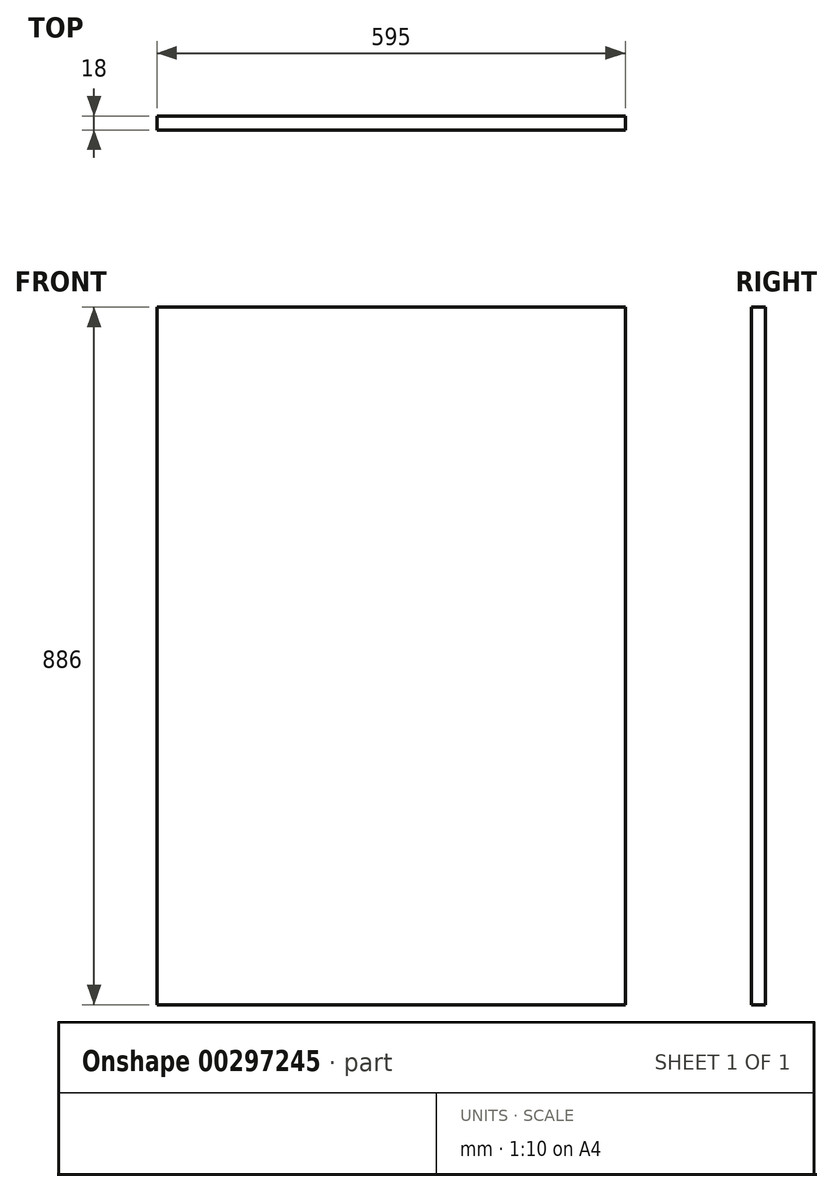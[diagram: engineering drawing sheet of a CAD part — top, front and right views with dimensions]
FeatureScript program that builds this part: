
annotation { "Feature Type Name" : "Feature", "Feature Type Description" : "" }
export const myFeature = defineFeature(function(context is Context, id is Id, definition is map)
    precondition{}
    {
        {
            var Q0;
            Q0=qCreatedBy(makeId("Front.planeOp"),FACE);
            var sketch = newSketch(context, id + "F0", { "sketchPlane" : qUnion([Q0])});
            skLineSegment(sketch, "E0.bottom", {"start": v(297.5, 443) * mm, "end": v(-297.5, 443) * mm});
            skLineSegment(sketch, "E0.top", {"start": v(297.5, -443) * mm, "end": v(-297.5, -443) * mm});
            skLineSegment(sketch, "E0.left", {"start": v(297.5, 443) * mm, "end": v(297.5, -443) * mm});
            skLineSegment(sketch, "E0.right", {"start": v(-297.5, 443) * mm, "end": v(-297.5, -443) * mm});
            skPoint(sketch, "E0.middle", {"position": v(0, 0) * mm});
            skSolve(sketch);
        }
        {
            var Q0;
            Q0 = qSketchRegion(id + "F0", true);
            extrude(context, id + "F1", {"entities" : qUnion([Q0]), "depth" : 18 * mm});
        }
    });
